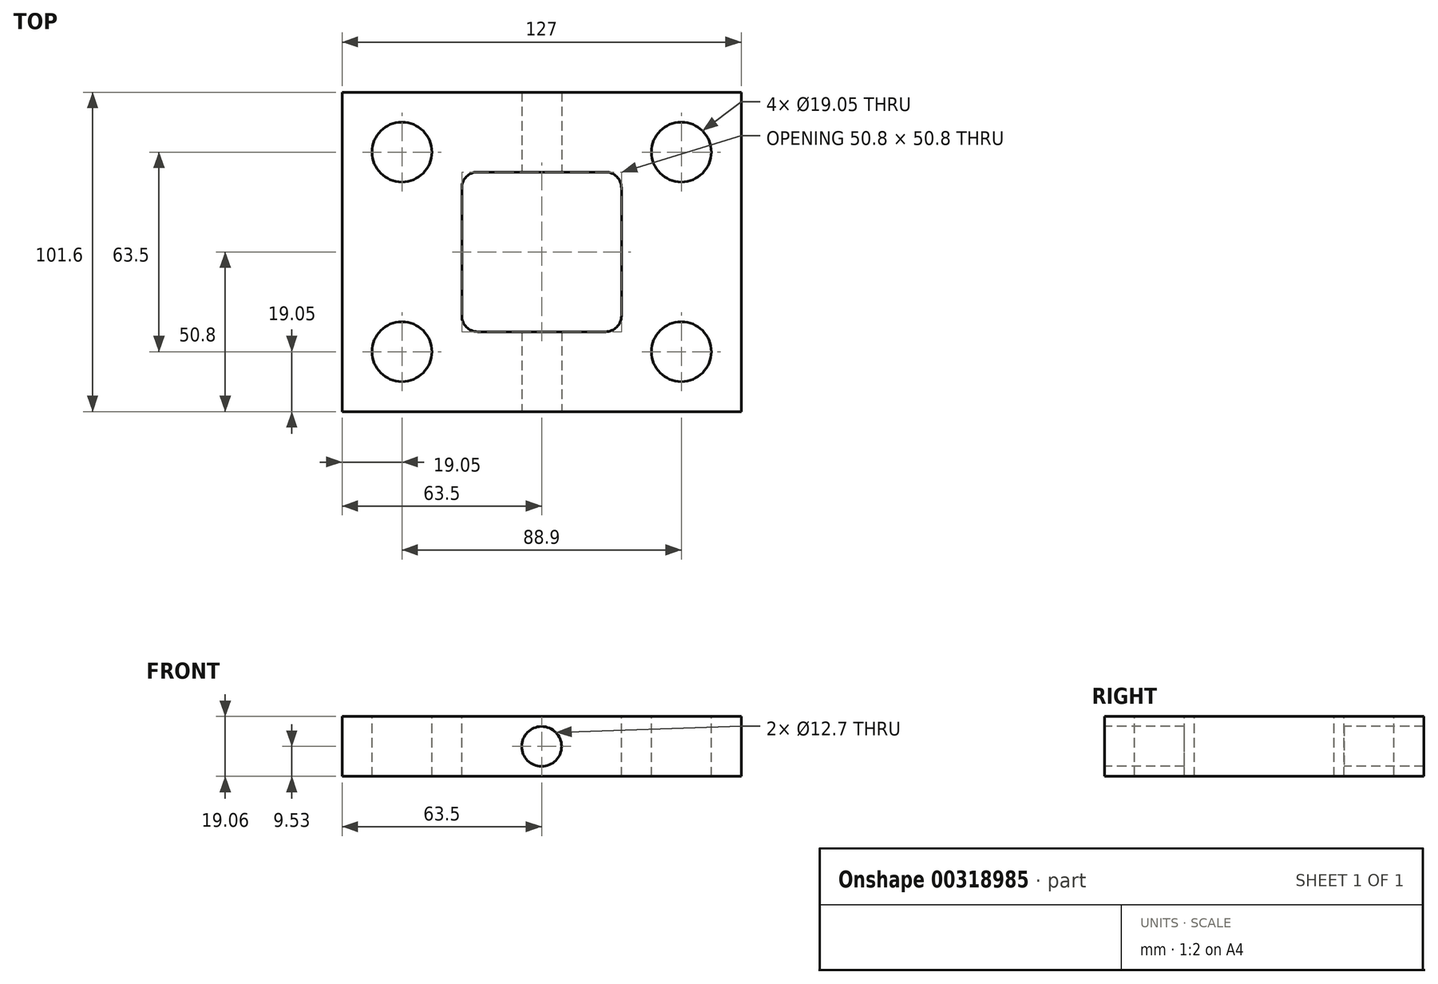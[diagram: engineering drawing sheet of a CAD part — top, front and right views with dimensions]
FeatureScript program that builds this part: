
annotation { "Feature Type Name" : "Feature", "Feature Type Description" : "" }
export const myFeature = defineFeature(function(context is Context, id is Id, definition is map)
    precondition{}
    {
        {
            var Q0;
            Q0=qCreatedBy(makeId("Top.planeOp"),FACE);
            var sketch = newSketch(context, id + "F0", { "sketchPlane" : qUnion([Q0])});
            skLineSegment(sketch, "E0.bottom", {"start": v(-63.5, 50.8) * mm, "end": v(63.5, 50.8) * mm});
            skLineSegment(sketch, "E0.top", {"start": v(-63.5, -50.8) * mm, "end": v(63.5, -50.8) * mm});
            skLineSegment(sketch, "E0.left", {"start": v(-63.5, 50.8) * mm, "end": v(-63.5, -50.8) * mm});
            skLineSegment(sketch, "E0.right", {"start": v(63.5, 50.8) * mm, "end": v(63.5, -50.8) * mm});
            skPoint(sketch, "E0.middle", {"position": v(0, 0) * mm});
            skSolve(sketch);
        }
        {
            var Q0;
            Q0 = qSketchRegion(id + "F0", true);
            extrude(context, id + "F1", {"entities" : qUnion([Q0]), "depth" : 9.52 * mm});
        }
        {
            var Q0;
            Q0=makeQuery(id+"F1.opExtrude","CAP_FACE",FACE,{"disambiguationData":[OSD([sQuery(id+"F0.wireOp",EDGE,"E0.bottom"),sQuery(id+"F0.wireOp",EDGE,"E0.top"),sQuery(id+"F0.wireOp",EDGE,"E0.left"),sQuery(id+"F0.wireOp",EDGE,"E0.right")])],"isStart":true});
            extrude(context, id + "F2", {"entities" : qUnion([Q0]), "operationType" : NewBodyOperationType.ADD, "depth" : 9.52 * mm});
        }
        {
            var Q0;
            Q0=makeQuery(id+"F1.opExtrude","CAP_FACE",FACE,{"disambiguationData":[OSD([sQuery(id+"F0.wireOp",EDGE,"E0.bottom"),sQuery(id+"F0.wireOp",EDGE,"E0.top"),sQuery(id+"F0.wireOp",EDGE,"E0.left"),sQuery(id+"F0.wireOp",EDGE,"E0.right")])],"isStart":false});
            var sketch = newSketch(context, id + "F3", { "sketchPlane" : qUnion([Q0])});
            skCircle(sketch, "E1", {"center": v(-44.45, -31.75) * mm, "radius": 9.53 * mm});
            skCircle(sketch, "E2", {"center": v(-44.45, 31.75) * mm, "radius": 9.53 * mm});
            skCircle(sketch, "E3", {"center": v(44.45, -31.75) * mm, "radius": 9.53 * mm});
            skCircle(sketch, "E4", {"center": v(44.45, 31.75) * mm, "radius": 9.53 * mm});
            skLineSegment(sketch, "E5", {"start": v(25.4, -25.4) * mm, "end": v(25.4, 25.4) * mm});
            skLineSegment(sketch, "E6", {"start": v(25.4, 25.4) * mm, "end": v(-25.4, 25.4) * mm});
            skLineSegment(sketch, "E7", {"start": v(-25.4, 25.4) * mm, "end": v(-25.4, -25.4) * mm});
            skLineSegment(sketch, "E8", {"start": v(-25.4, -25.4) * mm, "end": v(25.4, -25.4) * mm});
            skSolve(sketch);
        }
        {
            var Q0;
            Q0=makeQuery(id+"F3.imprint","IMPRINT",FACE,{"disambiguationData":[TD([[makeQuery(id+"F3.imprint","IMPRINT",EDGE,{"derivedFrom":sQuery(id+"F3.wireOp",EDGE,"E5")}),1.0]])]});
            var Q1;
            Q1=makeQuery(id+"F3.imprint","IMPRINT",FACE,{"disambiguationData":[TD([[makeQuery(id+"F3.imprint","IMPRINT",EDGE,{"derivedFrom":sQuery(id+"F3.wireOp",EDGE,"E1")}),1.0]])]});
            var Q2;
            Q2=makeQuery(id+"F3.imprint","IMPRINT",FACE,{"disambiguationData":[TD([[makeQuery(id+"F3.imprint","IMPRINT",EDGE,{"derivedFrom":sQuery(id+"F3.wireOp",EDGE,"E2")}),1.0]])]});
            var Q3;
            Q3=makeQuery(id+"F3.imprint","IMPRINT",FACE,{"disambiguationData":[TD([[makeQuery(id+"F3.imprint","IMPRINT",EDGE,{"derivedFrom":sQuery(id+"F3.wireOp",EDGE,"E4")}),1.0]])]});
            var Q4;
            Q4=makeQuery(id+"F3.imprint","IMPRINT",FACE,{"disambiguationData":[TD([[makeQuery(id+"F3.imprint","IMPRINT",EDGE,{"derivedFrom":sQuery(id+"F3.wireOp",EDGE,"E3")}),1.0]])]});
            extrude(context, id + "F4", {"entities" : qUnion([Q0, Q1, Q2, Q3, Q4]), "operationType" : NewBodyOperationType.REMOVE, "oppositeDirection" : true, "depth" : 25.4 * mm});
        }
        {
            var Q0;
            Q0=makeQuery(id+"F4.boolean.opBoolean","COPY",EDGE,{"derivedFrom":makeQuery(id+"F4.opExtrude","SWEPT_EDGE",EDGE,{"disambiguationData":[OSD([sQuery(id+"F3.wireOp",EDGE,"E6"),sQuery(id+"F3.wireOp",EDGE,"E7")])]})});
            var Q1;
            Q1=makeQuery(id+"F4.boolean.opBoolean","COPY",EDGE,{"derivedFrom":makeQuery(id+"F4.opExtrude","SWEPT_EDGE",EDGE,{"disambiguationData":[OSD([sQuery(id+"F3.wireOp",EDGE,"E7"),sQuery(id+"F3.wireOp",EDGE,"E8")])]})});
            var Q2;
            Q2=makeQuery(id+"F4.boolean.opBoolean","COPY",EDGE,{"derivedFrom":makeQuery(id+"F4.opExtrude","SWEPT_EDGE",EDGE,{"disambiguationData":[OSD([sQuery(id+"F3.wireOp",EDGE,"E5"),sQuery(id+"F3.wireOp",EDGE,"E8")])]})});
            var Q3;
            Q3=makeQuery(id+"F4.boolean.opBoolean","COPY",EDGE,{"derivedFrom":makeQuery(id+"F4.opExtrude","SWEPT_EDGE",EDGE,{"disambiguationData":[OSD([sQuery(id+"F3.wireOp",EDGE,"E5"),sQuery(id+"F3.wireOp",EDGE,"E6")])]})});
            fillet(context, id + "F5", {"entities" : qUnion([Q0, Q1, Q2, Q3]), "radius" : 5.08 * mm, "tangentPropagation" : true, "allowEdgeOverflow" : false});
        }
        {
            var Q0;
            {var subQ0=sQuery(id+"F0.wireOp",EDGE,"E0.top");Q0=makeQuery(id+"F2.boolean.opBoolean","MERGE",FACE,{"derivedFrom":[makeQuery(id+"F1.opExtrude","SWEPT_FACE",FACE,{"disambiguationData":[OSD([subQ0])]}),makeQuery(id+"F2.opExtrude","SWEPT_FACE",FACE,{"disambiguationData":[OSD([subQ0])]})]});}
            var sketch = newSketch(context, id + "F6", { "sketchPlane" : qUnion([Q0])});
            skCircle(sketch, "E9", {"center": v(0, 0) * mm, "radius": 6.35 * mm});
            skSolve(sketch);
        }
        {
            var Q0;
            Q0 = qSketchRegion(id + "F6", true);
            extrude(context, id + "F7", {"entities" : qUnion([Q0]), "operationType" : NewBodyOperationType.REMOVE, "oppositeDirection" : true, "depth" : 116.08 * mm});
        }
    });
